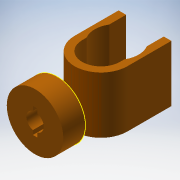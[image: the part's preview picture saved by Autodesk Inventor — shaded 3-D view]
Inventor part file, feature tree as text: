
AUTODESK INVENTOR PART (.ipt)
format: ipt  version: 2018 (Build 220112000, 112)  size: 187,904 bytes
history: native  units: mm
features: extrude x6, sketch x5, fillet x2
ambient origin geometry x8: Origin, YZ Plane, XZ Plane, XY Plane, X Axis, Y Axis, Z Axis, Center Point
bodies: Solid1 (feature_tree)
feature tree (13):
  extrude  "Extrusion1"  Depth=9.0mm
  extrude  "Extrusion5"  Depth=3.5mm
  extrude  "Extrusion6"  Depth=7.3mm
  extrude  "Extrusion2"  Depth=8.0mm TaperAngle=0.0deg
  sketch  "Sketch3"  dims[d7=18.0mm d8=0.0mm d9=7.3mm]
  extrude  "Extrusion3"  Depth=3.0mm
  extrude  "Extrusion4"  Depth=3.0mm
  fillet  "Fillet1"  Radius=0.26mm
  fillet  "Fillet2"  Radius=0.7mm
  sketch  "Sketch1"  dims[d1=2.23mm d3=9.0mm]
  sketch  "Sketch2"  dims[d4=3.5mm d5=0.0mm d6=2.0mm]
  sketch  "Sketch4"  dims[d10=2.0mm d11=8.0mm d12=0.0mm]
  sketch  "Sketch8"  dims[d13=12.0mm d14=0.0mm d15=1.0mm d16=1.0mm d18=0.26mm d19=0.7mm d20=4.0mm d21=3.0mm d23=1.2mm d24=7.0mm d25=7.0mm d26=7.0mm d27=2.5mm d28=9.0mm d29=0.0mm d33=8.0mm d34=9.0mm d35=0.0mm]
